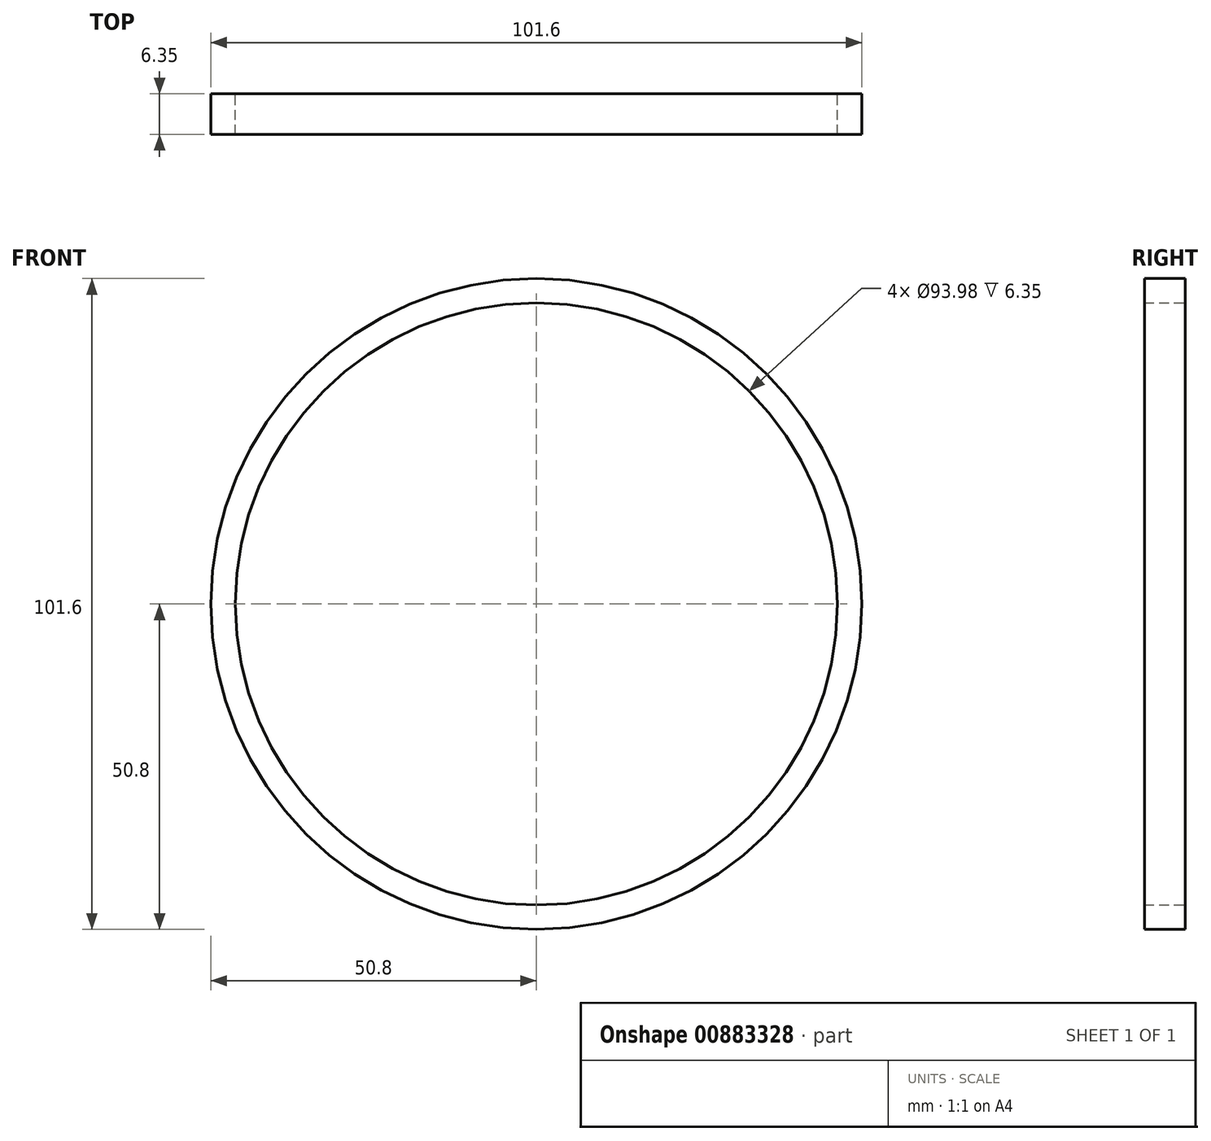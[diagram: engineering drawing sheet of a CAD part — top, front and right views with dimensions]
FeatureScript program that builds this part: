
annotation { "Feature Type Name" : "Feature", "Feature Type Description" : "" }
export const myFeature = defineFeature(function(context is Context, id is Id, definition is map)
    precondition{}
    {
        {
            var Q0;
            Q0=qCreatedBy(makeId("Front.planeOp"),FACE);
            var sketch = newSketch(context, id + "F0", { "sketchPlane" : qUnion([Q0])});
            skCircle(sketch, "E0", {"center": v(0, 0) * mm, "radius": 50.8 * mm});
            skCircle(sketch, "E1", {"center": v(0, 0) * mm, "radius": 47 * mm});
            skSolve(sketch);
        }
        {
            var Q0;
            Q0=makeQuery(id+"F0.imprint","IMPRINT",FACE,{"disambiguationData":[TD([[makeQuery(id+"F0.imprint","IMPRINT",EDGE,{"derivedFrom":sQuery(id+"F0.wireOp",EDGE,"E0")}),1.0]])]});
            extrude(context, id + "F1", {"entities" : qUnion([Q0]), "depth" : 6.35 * mm, "offsetDistance" : 25.4 * mm});
        }
    });
